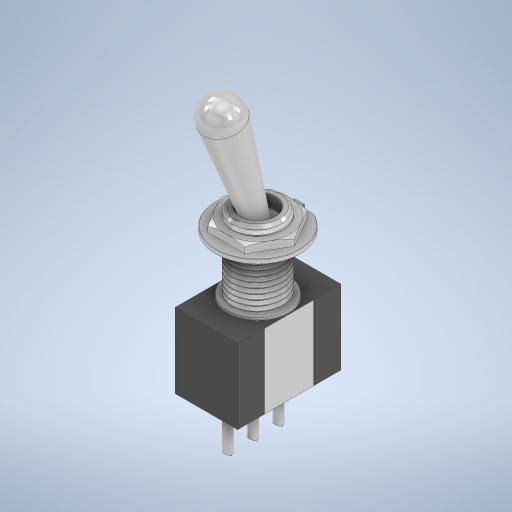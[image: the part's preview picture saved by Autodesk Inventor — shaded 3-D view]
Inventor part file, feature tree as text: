
AUTODESK INVENTOR PART (.ipt)
format: ipt  version: 2024 (Build 280153000, 153)  size: 854,016 bytes
history: native  units: in
note: dims shown in document units (in); Inventor stores cm internally (conversion verified against a paired STEP export)
features: other x7, fillet x2, mirror x1, revolve x1
ambient origin geometry x8: Origin, YZ Plane, XZ Plane, XY Plane, X Axis, Y Axis, Z Axis, Center Point
bodies: Solid1 (feature_tree), Solid2 (feature_tree), Solid3 (feature_tree), Solid4 (feature_tree), Solid5 (feature_tree), Solid6 (feature_tree), Solid7 (feature_tree), Solid8 (feature_tree), Solid9 (feature_tree), Solid10 (feature_tree), Solid11 (feature_tree)
feature tree (11):
  other  "Cut-Extrude2"
  fillet  "Fillet3"  [1 undecoded]
  other  "Cut-Sweep5"
  fillet  "Fillet1"  [1 undecoded]
  other  "Cut-Extrude5"
  mirror  "Mirror2"
  other  "LPattern1[1]"
  other  "LPattern1[2]"
  other  "LPattern1[3]"
  other  "LPattern1[4]"
  revolve  "Revolve2"  [1 undecoded]
note: 3 required parameter values undecoded (feature->parameter linkage not recoverable at this tier; creation-order binding heuristic only, values carry confidence <= 0.55)
